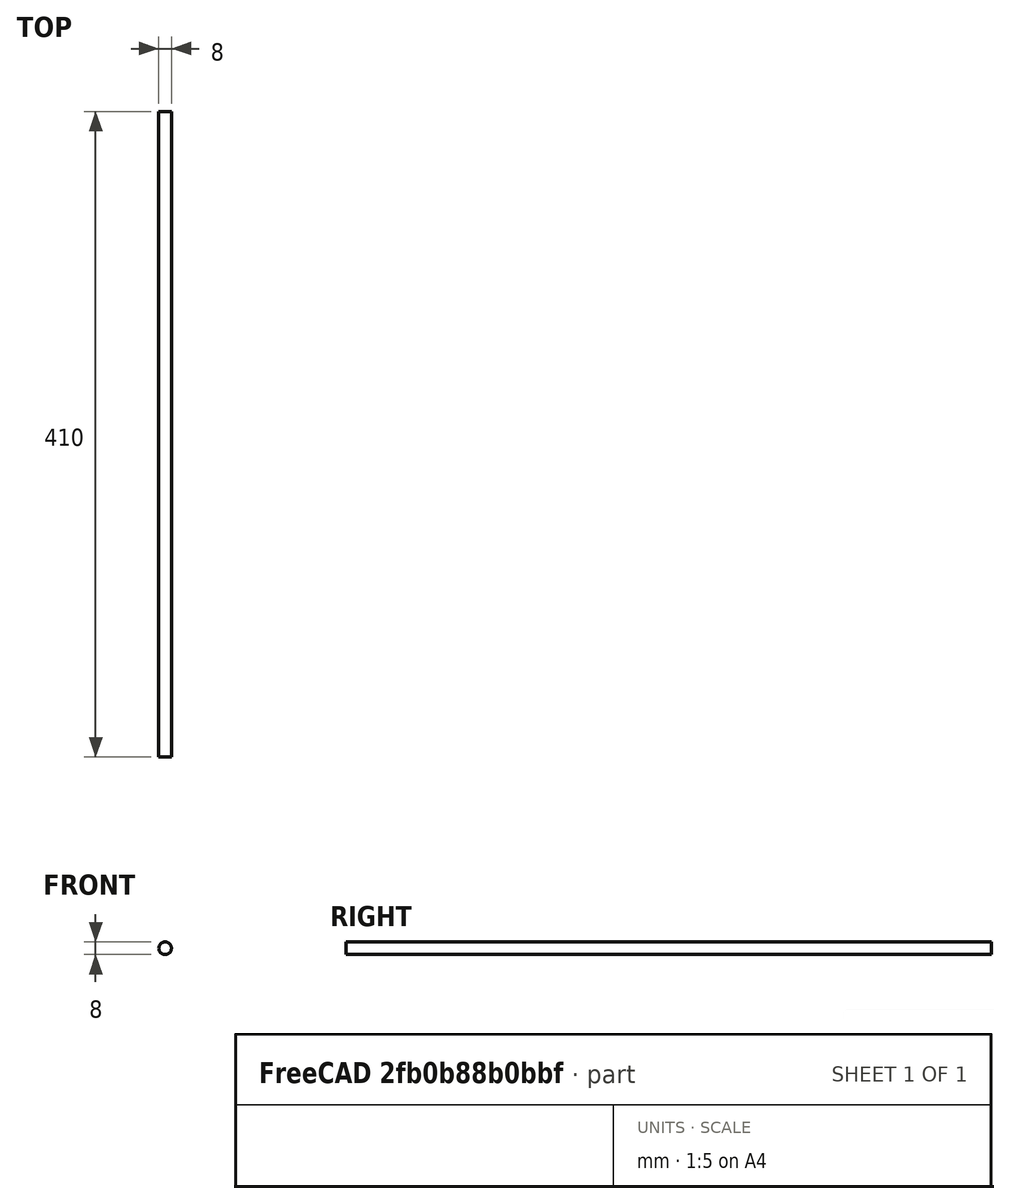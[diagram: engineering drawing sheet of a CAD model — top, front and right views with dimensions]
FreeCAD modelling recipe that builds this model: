
FCSTD DOCUMENT  (FreeCAD 2023.521R14555 (Git shallow))
Label: Y_8mm
License: All rights reserved
objects: PartDesign::CoordinateSystem×2, Sketcher::SketchObject×1, PartDesign::Pad×1, PartDesign::Body×1, App::Part×1
note: 8 computed .brp shape members not serialized (recipe doc carries the construction recipe); baked Part::Feature solids carry a one-line shape summary decoded from their .brp

FEATURE [Sketcher::SketchObject] Sketch
  ArcFitTolerance = 1e-06
  AttachmentSupport = -> [XZ_Plane]
  ExternalBSplineMaxDegree = 5
  ExternalBSplineTolerance = 0.0001
  FullyConstrained = true
  InternalTolerance = 1e-06
  InvalidShape = false
  MakeInternals = false
  MapMode = 5
  Placement = pos=(0,0,0) rot=(1,0,0;1.5708rad)
  Support = -> [XZ_Plane]
  TreeRank = 14
  ValidateShape = false
  sketch-geometry (1):
    g0: Circle CenterX=0 CenterY=0 CenterZ=0 NormalX=0 NormalY=0 NormalZ=1 AngleXU=0 Radius=4
  constraints (2):
    c: Coincident(g0,g-1)
    c: Diameter(g0) = 8
FEATURE [PartDesign::Pad] Pad
  AddSubType = 0
  AlongSketchNormal = false
  AutoTaperInnerAngle = true
  CheckUpToFaceLimits = true
  ClaimChildren = false
  Direction = (0,-1,2e-16)
  Fit = 0
  FitJoin = 0
  InnerFit = 0
  InnerFitJoin = 0
  InvalidShape = false
  Length = 410
  Length2 = 10
  Linearize = true
  NewSolid = false
  Profile = -> Sketch
  ReferenceAxis = -> Sketch [N_Axis]
  Suppress = false
  TaperInnerAngle = 0
  TaperInnerAngleRev = 0
  TreeRank = 15
  Type = 0
  ValidateShape = true
  _ProfileBasedVersion = 1
FEATURE [PartDesign::Body] Body
  AutoGroupSolids = false
  ClaimAllChildren = false
  ExportMode = 0
  Group = -> [Sketch,Pad]
  InvalidShape = false
  Origin = -> Origin001
  Tip = -> Pad
  TreeRank = 13
  ValidateShape = false
  _ExportChildren = -> [Pad]
  _GroupVersion = 1
FEATURE [PartDesign::CoordinateSystem] Local_CS  label="Start"
  AttacherType = Attacher::AttachEngine3D
  AttachmentSupport = -> [Pad]
  InvalidShape = false
  MapMode = 11
  Placement = pos=(0,0,0) rot=(0.57735,-0.57735,0.57735;2.0944rad)
  Support = -> [Pad]
  TreeRank = 16
  ValidateShape = false
FEATURE [PartDesign::CoordinateSystem] Local_CS001  label="End"
  AttacherType = Attacher::AttachEngine3D
  AttachmentSupport = -> [Pad]
  InvalidShape = false
  MapMode = 11
  Placement = pos=(0,-410,9.1e-14) rot=(0.57735,-0.57735,0.57735;2.0944rad)
  Support = -> [Pad]
  TreeRank = 17
  ValidateShape = false
FEATURE [App::Part] Part  label="Y_Rod"
  ClaimAllChildren = false
  ExportMode = 1
  Group = -> [Body,Local_CS,Local_CS001]
  Origin = -> Origin
  TreeRank = 3
  _ExportChildren = -> [Body,Local_CS,Local_CS001]
  _GroupVersion = 1
